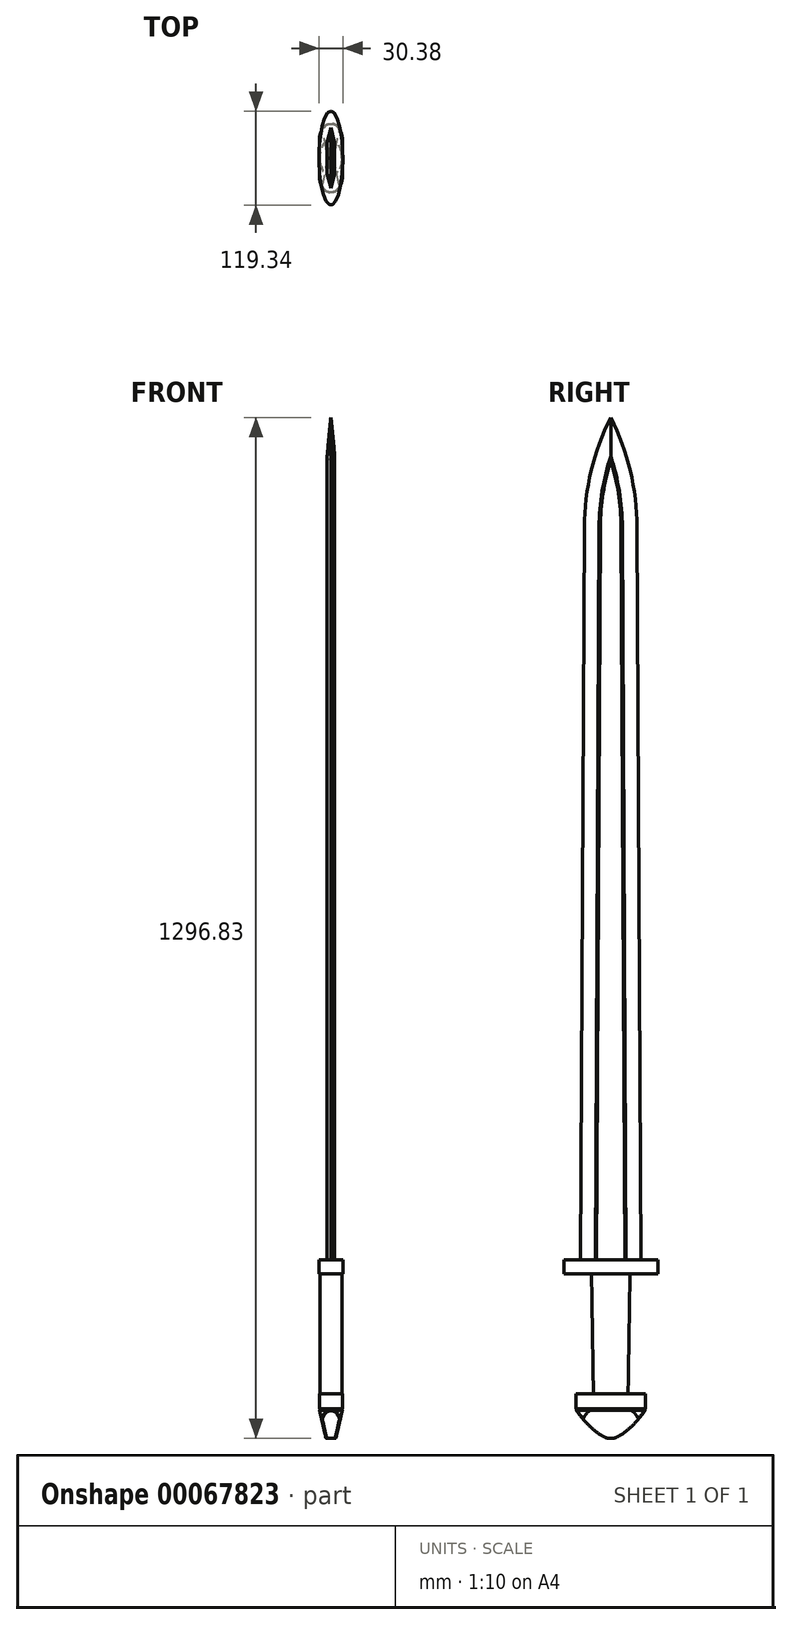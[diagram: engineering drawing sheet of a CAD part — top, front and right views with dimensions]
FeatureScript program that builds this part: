
annotation { "Feature Type Name" : "Feature", "Feature Type Description" : "" }
export const myFeature = defineFeature(function(context is Context, id is Id, definition is map)
    precondition{}
    {
        {
            var Q0;
            Q0=qCreatedBy(makeId("Top.planeOp"),FACE);
            var sketch = newSketch(context, id + "F0", { "sketchPlane" : qUnion([Q0])});
            skEllipse(sketch, "E0", {"center": v(0, 0) * mm, "majorRadius": 22.01 * mm, "minorRadius": 14.03 * mm, "majorAxis": v(0, 1)});
            skSolve(sketch);
        }
        {
            var Q0;
            Q0=makeQuery(id+"F0.imprint","IMPRINT",FACE,{"disambiguationData":[TD([[makeQuery(id+"F0.imprint","IMPRINT",EDGE,{"derivedFrom":sQuery(id+"F0.wireOp",EDGE,"E0")}),1.0]])]});
            cPlane(context, id + "F1", {"entities" : qUnion([Q0]), "cplaneType" : CPlaneType.OFFSET, "offset" : 152.4 * mm, "width" : 152.4 * mm, "height" : 152.4 * mm});
        }
        {
            var Q0;
            Q0=qCreatedBy(id+"F1.planeOp",FACE);
            var sketch = newSketch(context, id + "F2", { "sketchPlane" : qUnion([Q0])});
            skEllipse(sketch, "E1", {"center": v(0, 0) * mm, "majorRadius": 24.49 * mm, "minorRadius": 14.02 * mm, "majorAxis": v(0, 1)});
            skSolve(sketch);
        }
        {
            var Q0;
            Q0=makeQuery(id+"F0.imprint","IMPRINT",FACE,{"disambiguationData":[TD([[makeQuery(id+"F0.imprint","IMPRINT",EDGE,{"derivedFrom":sQuery(id+"F0.wireOp",EDGE,"E0")}),1.0]])]});
            var Q1;
            Q1=makeQuery(id+"F2.imprint","IMPRINT",FACE,{"disambiguationData":[TD([[makeQuery(id+"F2.imprint","IMPRINT",EDGE,{"derivedFrom":sQuery(id+"F2.wireOp",EDGE,"E1")}),1.0]])]});
            loft(context, id + "F3", {"sheetProfilesArray" : [{ "sheetProfileEntities" : qUnion([Q0]) }, { "sheetProfileEntities" : qUnion([Q1]) }]});
        }
        {
            var Q0;
            Q0=makeQuery(id+"F3.opLoft","CAP_FACE",FACE,{"disambiguationData":[OSD([makeQuery(id+"F2.imprint","IMPRINT",FACE,{"disambiguationData":[TD([[makeQuery(id+"F2.imprint","IMPRINT",EDGE,{"derivedFrom":sQuery(id+"F2.wireOp",EDGE,"E1")}),1.0]])]})])],"isStart":true});
            var sketch = newSketch(context, id + "F4", { "sketchPlane" : qUnion([Q0])});
            skEllipse(sketch, "E2", {"center": v(0, 0) * mm, "majorRadius": 50.25 * mm, "minorRadius": 14.05 * mm, "majorAxis": v(0, 1)});
            skEllipse(sketch, "E3", {"center": v(0, 0) * mm, "majorRadius": 59.67 * mm, "minorRadius": 15.2 * mm, "majorAxis": v(0, 1)});
            skSolve(sketch);
        }
        {
            var Q0;
            Q0 = qSketchRegion(id + "F4", true);
            var Q1;
            Q1=makeQuery(id+"F4.imprint","IMPRINT",FACE,{"disambiguationData":[TD([[makeQuery(id+"F4.imprint","IMPRINT",EDGE,{"derivedFrom":sQuery(id+"F4.wireOp",EDGE,"E2")}),1.0]])]});
            var Q2;
            Q2=makeQuery(id+"F4.imprint","IMPRINT",FACE,{"disambiguationData":[TD([[makeQuery(id+"F4.imprint","IMPRINT",EDGE,{"derivedFrom":makeQuery(id+"F3.opLoft","MID_CAP_EDGE",EDGE,{"disambiguationData":[OSD([sQuery(id+"F0.wireOp",EDGE,"E0"),sQuery(id+"F2.wireOp",EDGE,"E1")])],"capPos":1.0})}),1.0]])]});
            extrude(context, id + "F5", {"entities" : qUnion([Q0, Q1, Q2]), "depth" : 17.78 * mm});
        }
        {
            var Q0;
            Q0=makeQuery(id+"F3.opLoft","CAP_FACE",FACE,{"disambiguationData":[OSD([makeQuery(id+"F0.imprint","IMPRINT",FACE,{"disambiguationData":[TD([[makeQuery(id+"F0.imprint","IMPRINT",EDGE,{"derivedFrom":sQuery(id+"F0.wireOp",EDGE,"E0")}),1.0]])]})])],"isStart":true});
            var sketch = newSketch(context, id + "F6", { "sketchPlane" : qUnion([Q0])});
            skLineSegment(sketch, "E4.rect.left", {"start": v(-14.65, 22.86) * mm, "end": v(-14.65, -22.86) * mm});
            skLineSegment(sketch, "E4.rect.right", {"start": v(14.65, 22.86) * mm, "end": v(14.65, -22.86) * mm});
            skPoint(sketch, "E4.rect.middle", {"position": v(0, 0) * mm});
            skPoint(sketch, "E5.rect.middle", {"position": v(-14.65, 22.86) * mm});
            skEllipticalArc(sketch, "E6", {});
            skLineSegment(sketch, "E7", {"start": v(0, 0) * mm, "end": v(-5.94, 0) * mm});
            skEllipticalArc(sketch, "E8.MirrorCS", {});
            skPoint(sketch, "E5.rect.right.end.orphan", {"position": v(-43.96, 22.86) * mm});
            skPoint(sketch, "E5.rect.right.start.orphan", {"position": v(-47.78, 25.4) * mm});
            skPoint(sketch, "E5.rect.left.end.orphan", {"position": v(18.47, 20.32) * mm});
            const initialGuessF6  = {"E6": [0, 0.02286, -1, 0, 0.014653067193173231, 0.021324570960949005, 3.141592653589793, 6.283185307179586], "E8.MirrorCS": [0, -0.02286, -1, 0, 0.014653067193173231, 0.021324570960949005, 6.283185307179586, 3.141592653589793]};
            skSetInitialGuess(sketch, initialGuessF6);
            skSolve(sketch);
        }
        {
            var Q0;
            Q0 = qSketchRegion(id + "F6", true);
            extrude(context, id + "F7", {"entities" : qUnion([Q0]), "depth" : 20.32 * mm});
        }
        {
            var Q0;
            Q0=qCreatedBy(makeId("Right.planeOp"),FACE);
            var sketch = newSketch(context, id + "F8", { "sketchPlane" : qUnion([Q0])});
            skLineSegment(sketch, "E9.0", {"start": v(-44.18, -20.32) * mm, "end": v(-22.86, -20.32) * mm});
            skLineSegment(sketch, "E10.0", {"start": v(22.86, -20.32) * mm, "end": v(44.18, -20.32) * mm});
            skLineSegment(sketch, "E11", {"start": v(0, 0) * mm, "end": v(0, -64.5) * mm});
            skLineSegment(sketch, "E12", {"start": v(-10.54, -53.96) * mm, "end": v(-44.18, -20.32) * mm});
            skLineSegment(sketch, "E13", {"start": v(10.54, -53.96) * mm, "end": v(44.18, -20.32) * mm});
            skArc(sketch, "E14", {"start": v(-44.18, -20.32) * mm, "mid": v(-29.18, -38.96) * mm, "end": v(-10.54, -53.96) * mm});
            skArc(sketch, "E15.MirrorCS", {"start": v(44.18, -20.32) * mm, "mid": v(29.18, -38.96) * mm, "end": v(10.54, -53.96) * mm});
            skArc(sketch, "E16", {"start": v(-10.54, -53.96) * mm, "mid": v(0, -56.86) * mm, "end": v(10.54, -53.96) * mm});
            skLineSegment(sketch, "E17", {"start": v(-22.86, -20.32) * mm, "end": v(22.86, -20.32) * mm});
            skSolve(sketch);
        }
        {
            var Q0;
            Q0 = qSketchRegion(id + "F8", true);
            extrude(context, id + "F9", {"entities" : qUnion([Q0]), "operationType" : NewBodyOperationType.ADD, "endBound" : BoundingType.SYMMETRIC, "depth" : 29.46 * mm});
        }
        {
            var Q0;
            Q0=qCreatedBy(makeId("Front.planeOp"),FACE);
            cPlane(context, id + "F10", {"entities" : qUnion([Q0]), "cplaneType" : CPlaneType.OFFSET, "offset" : 152.4 * mm, "width" : 152.4 * mm, "height" : 152.4 * mm});
        }
        {
            var Q0;
            Q0=qCreatedBy(id+"F10.planeOp",FACE);
            var sketch = newSketch(context, id + "F11", { "sketchPlane" : qUnion([Q0])});
            skLineSegment(sketch, "E18.0", {"start": v(14.73, -20.32) * mm, "end": v(0, -20.32) * mm});
            skLineSegment(sketch, "E19", {"start": v(17.78, -56.86) * mm, "end": v(-17.78, -56.86) * mm});
            skLineSegment(sketch, "E20.0", {"start": v(0, -20.32) * mm, "end": v(-14.73, -20.32) * mm});
            skLineSegment(sketch, "E21", {"start": v(-17.78, -56.86) * mm, "end": v(-10.55, -20.32) * mm});
            skLineSegment(sketch, "E22", {"start": v(0, -20.32) * mm, "end": v(0, -24.34) * mm});
            skLineSegment(sketch, "E23.MirrorCS", {"start": v(17.78, -56.86) * mm, "end": v(10.55, -20.32) * mm});
            skPoint(sketch, "E24", {"position": v(-7.37, -20.32) * mm});
            skLineSegment(sketch, "E25.0", {"start": v(-14.73, -20.32) * mm, "end": v(-14.73, -53.96) * mm});
            skLineSegment(sketch, "E26.0", {"start": v(-14.73, -53.96) * mm, "end": v(-14.73, -56.86) * mm});
            skLineSegment(sketch, "E27.0", {"start": v(14.73, -53.96) * mm, "end": v(14.73, -56.86) * mm});
            skLineSegment(sketch, "E28.0", {"start": v(14.73, -20.32) * mm, "end": v(14.73, -53.96) * mm});
            skLineSegment(sketch, "E29", {"start": v(-14.73, -20.32) * mm, "end": v(-6.3, -56.86) * mm});
            skLineSegment(sketch, "E30.MirrorCS", {"start": v(14.73, -20.32) * mm, "end": v(6.3, -56.86) * mm});
            skSolve(sketch);
        }
        {
            var Q0;
            {var subQ0=sQuery(id+"F11.wireOp",EDGE,"E28.0");var subQ1=sQuery(id+"F11.wireOp",EDGE,"E23.MirrorCS");var subQ2=makeQuery(id+"F11.imprint","INTERSECT",VERTEX,{"derivedFrom":[subQ1,subQ0]});Q0=makeQuery(id+"F11.imprint","IMPRINT",FACE,{"disambiguationData":[TD([[makeQuery(id+"F11.imprint","IMPRINT",EDGE,{"disambiguationData":[TD([[subQ2,-1.0]])],"derivedFrom":subQ1}),-1.0]])]});}
            var Q1;
            {var subQ1=sQuery(id+"F11.wireOp",EDGE,"E27.0");Q1=makeQuery(id+"F11.imprint","IMPRINT",FACE,{"disambiguationData":[TD([[makeQuery(id+"F11.imprint","IMPRINT",EDGE,{"derivedFrom":subQ1}),-1.0]])]});}
            var Q2;
            {var subQ0=sQuery(id+"F11.wireOp",EDGE,"E26.0");Q2=makeQuery(id+"F11.imprint","IMPRINT",FACE,{"disambiguationData":[TD([[makeQuery(id+"F11.imprint","IMPRINT",EDGE,{"derivedFrom":subQ0}),1.0]])]});}
            var Q3;
            {var subQ0=sQuery(id+"F11.wireOp",EDGE,"E25.0");var subQ1=sQuery(id+"F11.wireOp",EDGE,"E21");var subQ2=makeQuery(id+"F11.imprint","INTERSECT",VERTEX,{"derivedFrom":[subQ1,subQ0]});Q3=makeQuery(id+"F11.imprint","IMPRINT",FACE,{"disambiguationData":[TD([[makeQuery(id+"F11.imprint","IMPRINT",EDGE,{"disambiguationData":[TD([[subQ2,-1.0]])],"derivedFrom":subQ1}),1.0]])]});}
            extrude(context, id + "F12", {"entities" : qUnion([Q0, Q1, Q2, Q3]), "operationType" : NewBodyOperationType.REMOVE, "endBound" : BoundingType.THROUGH_ALL, "oppositeDirection" : true, "depth" : 25.4 * mm});
        }
        {
            var Q0;
            Q0=makeQuery(id+"F7.opExtrude","CAP_FACE",FACE,{"disambiguationData":[OSD([sQuery(id+"F6.wireOp",EDGE,"E4.rect.left"),sQuery(id+"F6.wireOp",EDGE,"E4.rect.right"),sQuery(id+"F6.wireOp",EDGE,"E6"),sQuery(id+"F6.wireOp",EDGE,"E8.MirrorCS")])],"isStart":true});
            var sketch = newSketch(context, id + "F13", { "sketchPlane" : qUnion([Q0])});
            skLineSegment(sketch, "E31.0.0", {"start": v(-14.73, -44.18) * mm, "end": v(0, -44.18) * mm});
            skEllipticalArc(sketch, "E31.0.1", {});
            skLineSegment(sketch, "E31.0.2", {"start": v(-14.65, -22.86) * mm, "end": v(-14.65, 22.86) * mm});
            skEllipticalArc(sketch, "E31.0.3", {});
            skLineSegment(sketch, "E31.0.4", {"start": v(0, 44.18) * mm, "end": v(-14.73, 44.18) * mm});
            skLineSegment(sketch, "E31.0.5", {"start": v(-14.73, 44.18) * mm, "end": v(-14.73, -44.18) * mm});
            skLineSegment(sketch, "E32.0.0", {"start": v(14.65, 22.86) * mm, "end": v(14.65, -22.86) * mm});
            skEllipticalArc(sketch, "E32.0.1", {});
            skLineSegment(sketch, "E32.0.2", {"start": v(0, -44.18) * mm, "end": v(14.73, -44.18) * mm});
            skLineSegment(sketch, "E32.0.3", {"start": v(14.73, -44.18) * mm, "end": v(14.73, 44.18) * mm});
            skLineSegment(sketch, "E32.0.4", {"start": v(14.73, 44.18) * mm, "end": v(0, 44.18) * mm});
            skEllipticalArc(sketch, "E32.0.5", {});
            skEllipticalArc(sketch, "E33.0.0", {});
            skLineSegment(sketch, "E33.0.1", {"start": v(14.65, -22.86) * mm, "end": v(14.65, 22.86) * mm});
            skEllipticalArc(sketch, "E33.0.2", {});
            skLineSegment(sketch, "E33.0.3", {"start": v(-14.65, 22.86) * mm, "end": v(-14.65, -22.86) * mm});
            const initialGuessF13  = {"E31.0.1": [0, -0.02286, 0, 1, 0.021324570960949005, 0.014653067193173231, 1.5707963267948966, 3.141592653589793], "E31.0.3": [0, 0.02286, 0, 1, 0.021324570960949005, 0.014653067193173231, 0, 1.5707963267948966], "E32.0.1": [0, -0.02286, 0, 1, 0.021324570960949005, 0.014653067193173231, 3.141592653589793, 4.71238898038469], "E32.0.5": [0, 0.02286, 0, 1, 0.021324570960949005, 0.014653067193173231, 4.71238898038469, 0], "E33.0.0": [0, -0.02286, 0, 1, 0.021324570960949005, 0.014653067193173231, 1.5707963267948966, 4.71238898038469], "E33.0.2": [0, 0.02286, 0, 1, 0.021324570960949005, 0.014653067193173231, 4.71238898038469, 1.5707963267948966]};
            skSetInitialGuess(sketch, initialGuessF13);
            skSolve(sketch);
        }
        {
            var Q0;
            {var subQ3=sQuery(id+"F13.wireOp",EDGE,"E31.0.0");Q0=makeQuery(id+"F13.imprint","IMPRINT",FACE,{"disambiguationData":[TD([[makeQuery(id+"F13.imprint","IMPRINT",EDGE,{"derivedFrom":subQ3}),1.0]])]});}
            var Q1;
            {var subQ3=sQuery(id+"F13.wireOp",EDGE,"E32.0.2");Q1=makeQuery(id+"F13.imprint","IMPRINT",FACE,{"disambiguationData":[TD([[makeQuery(id+"F13.imprint","IMPRINT",EDGE,{"derivedFrom":subQ3}),1.0]])]});}
            extrude(context, id + "F14", {"entities" : qUnion([Q0, Q1]), "operationType" : NewBodyOperationType.REMOVE, "endBound" : BoundingType.THROUGH_ALL, "oppositeDirection" : true, "depth" : 25.4 * mm});
        }
        {
            var Q0;
            Q0=makeQuery(id+"F7.opExtrude","CAP_FACE",FACE,{"disambiguationData":[OSD([sQuery(id+"F6.wireOp",EDGE,"E4.rect.left"),sQuery(id+"F6.wireOp",EDGE,"E4.rect.right"),sQuery(id+"F6.wireOp",EDGE,"E6"),sQuery(id+"F6.wireOp",EDGE,"E8.MirrorCS")])],"isStart":true});
            cPlane(context, id + "F15", {"entities" : qUnion([Q0]), "cplaneType" : CPlaneType.OFFSET, "offset" : 20.32 * mm, "oppositeDirection" : true, "width" : 152.4 * mm, "height" : 152.4 * mm});
        }
        {
            var Q0;
            Q0=qCreatedBy(id+"F15.planeOp",FACE);
            var sketch = newSketch(context, id + "F16", { "sketchPlane" : qUnion([Q0])});
            skEllipticalArc(sketch, "E34.0.0", {});
            skLineSegment(sketch, "E34.0.1", {"start": v(14.65, -22.86) * mm, "end": v(14.65, 22.86) * mm});
            skEllipticalArc(sketch, "E34.0.2", {});
            skLineSegment(sketch, "E34.0.3", {"start": v(-14.65, 22.86) * mm, "end": v(-14.65, -22.86) * mm});
            skLineSegment(sketch, "E35", {"start": v(-14.65, 22.86) * mm, "end": v(14.65, 22.86) * mm});
            skLineSegment(sketch, "E36", {"start": v(14.65, -22.86) * mm, "end": v(-14.65, -22.86) * mm});
            skPoint(sketch, "E37", {"position": v(0, 44.18) * mm});
            skPoint(sketch, "E38", {"position": v(0, -44.18) * mm});
            skEllipse(sketch, "E39", {"center": v(0, 22.86) * mm, "majorRadius": 21.32 * mm, "minorRadius": 14.65 * mm, "majorAxis": v(0, 1)});
            skEllipse(sketch, "E40", {"center": v(0, -22.86) * mm, "majorRadius": 21.32 * mm, "minorRadius": 14.65 * mm, "majorAxis": v(0, -1)});
            skPoint(sketch, "E41", {"position": v(-14.65, 0) * mm});
            const initialGuessF16  = {"E34.0.0": [0, -0.02286, 0, 1, 0.021324570960949005, 0.014653067193173231, 1.5707963267948966, 4.71238898038469], "E34.0.2": [0, 0.02286, 0, 1, 0.021324570960949005, 0.014653067193173231, 4.71238898038469, 1.5707963267948966], "E34.0.0": [0, -0.02286, 0, 1, 0.021324570960949005, 0.014653067193173231, 1.5707963267948966, 4.71238898038469], "E34.0.2": [0, 0.02286, 0, 1, 0.021324570960949005, 0.014653067193173231, 4.71238898038469, 1.5707963267948966]};
            skSetInitialGuess(sketch, initialGuessF16);
            skSolve(sketch);
        }
        {
            var Q0;
            Q0=qCreatedBy(makeId("Front.planeOp"),FACE);
            var sketch = newSketch(context, id + "F17", { "sketchPlane" : qUnion([Q0])});
            skPoint(sketch, "E42.0", {"position": v(-14.65, -20.32) * mm});
            skCircle(sketch, "E43", {"center": v(-14.65, -20.32) * mm, "radius": 0.94 * mm});
            skPoint(sketch, "E44.0", {"position": v(14.65, -20.32) * mm});
            skCircle(sketch, "E45", {"center": v(14.65, -20.32) * mm, "radius": 0.94 * mm});
            skPoint(sketch, "E46.0", {"position": v(7.02, -20.73) * mm});
            skPoint(sketch, "E47.0", {"position": v(36.33, -20.73) * mm});
            skSolve(sketch);
        }
        {
            var Q0;
            Q0=qCreatedBy(makeId("Front.planeOp"),FACE);
            cPlane(context, id + "F18", {"entities" : qUnion([Q0]), "cplaneType" : CPlaneType.OFFSET, "offset" : 22.86 * mm, "width" : 152.4 * mm, "height" : 152.4 * mm});
        }
        {
            var Q0;
            Q0=qCreatedBy(id+"F18.planeOp",FACE);
            var sketch = newSketch(context, id + "F19", { "sketchPlane" : qUnion([Q0])});
            skCircle(sketch, "E48.0", {"center": v(-14.65, -20.32) * mm, "radius": 0.94 * mm});
            skSolve(sketch);
        }
        {
            var Q0;
            Q0=qCreatedBy(id+"F18.planeOp",FACE);
            cPlane(context, id + "F20", {"entities" : qUnion([Q0]), "cplaneType" : CPlaneType.OFFSET, "offset" : 45.72 * mm, "oppositeDirection" : true, "width" : 152.4 * mm, "height" : 152.4 * mm});
        }
        {
            var Q0;
            Q0=qCreatedBy(id+"F20.planeOp",FACE);
            var sketch = newSketch(context, id + "F21", { "sketchPlane" : qUnion([Q0])});
            skCircle(sketch, "E49.0", {"center": v(-14.65, -20.32) * mm, "radius": 0.94 * mm});
            skSolve(sketch);
        }
        {
            var Q0;
            Q0=makeQuery(id+"F21.imprint","IMPRINT",FACE,{"disambiguationData":[TD([[makeQuery(id+"F21.imprint","IMPRINT",EDGE,{"derivedFrom":sQuery(id+"F21.wireOp",EDGE,"E49.0")}),1.0]])]});
            var Q1;
            Q1=sQuery(id+"F16.wireOp",EDGE,"E34.0.2");
            sweep(context, id + "F22", {"operationType" : NewBodyOperationType.REMOVE, "profiles" : qUnion([Q0]), "path" : qUnion([Q1])});
        }
        {
            var Q0;
            Q0=makeQuery(id+"F19.imprint","IMPRINT",FACE,{"disambiguationData":[TD([[makeQuery(id+"F19.imprint","IMPRINT",EDGE,{"derivedFrom":sQuery(id+"F19.wireOp",EDGE,"E48.0")}),1.0]])]});
            var Q1;
            Q1=sQuery(id+"F16.wireOp",EDGE,"E34.0.0");
            sweep(context, id + "F23", {"operationType" : NewBodyOperationType.REMOVE, "profiles" : qUnion([Q0]), "path" : qUnion([Q1])});
        }
        {
            var Q0;
            Q0=makeQuery(id+"F17.imprint","IMPRINT",FACE,{"disambiguationData":[TD([[makeQuery(id+"F17.imprint","IMPRINT",EDGE,{"derivedFrom":sQuery(id+"F17.wireOp",EDGE,"E43")}),1.0]])]});
            extrude(context, id + "F24", {"entities" : qUnion([Q0]), "operationType" : NewBodyOperationType.REMOVE, "endBound" : BoundingType.SYMMETRIC, "oppositeDirection" : true, "depth" : 254 * mm});
        }
        {
            var Q0;
            Q0=makeQuery(id+"F17.imprint","IMPRINT",FACE,{"disambiguationData":[TD([[makeQuery(id+"F17.imprint","IMPRINT",EDGE,{"derivedFrom":sQuery(id+"F17.wireOp",EDGE,"E45")}),1.0]])]});
            extrude(context, id + "F25", {"entities" : qUnion([Q0]), "operationType" : NewBodyOperationType.REMOVE, "endBound" : BoundingType.SYMMETRIC, "depth" : 254 * mm});
        }
        {
            var Q0;
            Q0=qCreatedBy(makeId("Right.planeOp"),FACE);
            var sketch = newSketch(context, id + "F26", { "sketchPlane" : qUnion([Q0])});
            skArc(sketch, "E50.0", {"start": v(10.54, -53.96) * mm, "mid": v(0, -56.86) * mm, "end": v(-10.54, -53.96) * mm});
            skLineSegment(sketch, "E51.0", {"start": v(-59.67, 170.18) * mm, "end": v(59.67, 170.18) * mm});
            skLineSegment(sketch, "E52", {"start": v(0, 170.18) * mm, "end": v(0, 1109.98) * mm});
            skLineSegment(sketch, "E53", {"start": v(38.35, 170.18) * mm, "end": v(33.47, 1100.69) * mm});
            skLineSegment(sketch, "E54.MirrorCS", {"start": v(-38.35, 170.18) * mm, "end": v(-33.47, 1100.69) * mm});
            skLineSegment(sketch, "E55", {"start": v(0, 1109.98) * mm, "end": v(0, 1239.97) * mm});
            skArc(sketch, "E56", {"start": v(33.47, 1100.69) * mm, "mid": v(24.8, 1172.27) * mm, "end": v(0, 1239.97) * mm});
            skArc(sketch, "E57.MirrorCS", {"start": v(-33.47, 1100.69) * mm, "mid": v(-24.8, 1172.27) * mm, "end": v(0, 1239.97) * mm});
            skSolve(sketch);
        }
        {
            var Q0;
            Q0 = qSketchRegion(id + "F26", true);
            extrude(context, id + "F27", {"entities" : qUnion([Q0]), "endBound" : BoundingType.SYMMETRIC, "depth" : 10.16 * mm});
        }
        {
            var Q0;
            Q0=makeQuery(id+"F27.opExtrude","CAP_EDGE",EDGE,{"disambiguationData":[OSD([sQuery(id+"F26.wireOp",EDGE,"E53")])],"isStart":true});
            var Q1;
            Q1=makeQuery(id+"F27.opExtrude","CAP_EDGE",EDGE,{"disambiguationData":[OSD([sQuery(id+"F26.wireOp",EDGE,"E54.MirrorCS")])],"isStart":true});
            chamfer(context, id + "F28", {"entities" : qUnion([Q0, Q1]), "chamferType" : ChamferType.TWO_OFFSETS, "width1" : 5.08 * mm, "oppositeDirection" : false, "width2" : 20.32 * mm, "tangentPropagation" : true});
        }
        {
            var Q0;
            Q0=makeQuery(id+"F27.opExtrude","CAP_EDGE",EDGE,{"disambiguationData":[OSD([sQuery(id+"F26.wireOp",EDGE,"E54.MirrorCS")])],"isStart":false});
            var Q1;
            Q1=makeQuery(id+"F27.opExtrude","CAP_EDGE",EDGE,{"disambiguationData":[OSD([sQuery(id+"F26.wireOp",EDGE,"E53")])],"isStart":false});
            chamfer(context, id + "F29", {"entities" : qUnion([Q0, Q1]), "chamferType" : ChamferType.TWO_OFFSETS, "width1" : 5.08 * mm, "oppositeDirection" : false, "width2" : 20.32 * mm, "tangentPropagation" : true});
        }
        {
            var Q0;
            Q0=makeQuery(id+"F27.opExtrude","CAP_FACE",FACE,{"disambiguationData":[OSD([sQuery(id+"F26.wireOp",EDGE,"E51.0"),sQuery(id+"F26.wireOp",EDGE,"E53"),sQuery(id+"F26.wireOp",EDGE,"E54.MirrorCS"),sQuery(id+"F26.wireOp",EDGE,"E56"),sQuery(id+"F26.wireOp",EDGE,"E57.MirrorCS")])],"isStart":false});
            var sketch = newSketch(context, id + "F30", { "sketchPlane" : qUnion([Q0])});
            skLineSegment(sketch, "E58.0.0", {"start": v(-18.03, 170.18) * mm, "end": v(18.03, 170.18) * mm});
            skLineSegment(sketch, "E58.0.1", {"start": v(18.03, 170.18) * mm, "end": v(13.15, 1100.58) * mm});
            skArc(sketch, "E58.0.2", {"start": v(13.15, 1100.58) * mm, "mid": v(9.73, 1143.71) * mm, "end": v(0, 1185.87) * mm});
            skArc(sketch, "E58.0.3", {"start": v(0, 1185.87) * mm, "mid": v(-9.73, 1143.71) * mm, "end": v(-13.15, 1100.58) * mm});
            skLineSegment(sketch, "E58.0.4", {"start": v(-13.15, 1100.58) * mm, "end": v(-18.03, 170.18) * mm});
            skSolve(sketch);
        }
        {
            var Q0;
            Q0 = qSketchRegion(id + "F30", true);
            extrude(context, id + "F31", {"entities" : qUnion([Q0]), "operationType" : NewBodyOperationType.REMOVE, "oppositeDirection" : true, "depth" : 2.54 * mm});
        }
        {
            var Q0;
            Q0=makeQuery(id+"F27.opExtrude","CAP_FACE",FACE,{"disambiguationData":[OSD([sQuery(id+"F26.wireOp",EDGE,"E51.0"),sQuery(id+"F26.wireOp",EDGE,"E53"),sQuery(id+"F26.wireOp",EDGE,"E54.MirrorCS"),sQuery(id+"F26.wireOp",EDGE,"E56"),sQuery(id+"F26.wireOp",EDGE,"E57.MirrorCS")])],"isStart":true});
            var sketch = newSketch(context, id + "F32", { "sketchPlane" : qUnion([Q0])});
            skLineSegment(sketch, "E59.0.0", {"start": v(-18.03, 170.18) * mm, "end": v(18.03, 170.18) * mm});
            skLineSegment(sketch, "E59.0.1", {"start": v(18.03, 170.18) * mm, "end": v(13.15, 1100.58) * mm});
            skArc(sketch, "E59.0.2", {"start": v(13.15, 1100.58) * mm, "mid": v(9.73, 1143.71) * mm, "end": v(0, 1185.87) * mm});
            skArc(sketch, "E59.0.3", {"start": v(0, 1185.87) * mm, "mid": v(-9.73, 1143.71) * mm, "end": v(-13.15, 1100.58) * mm});
            skLineSegment(sketch, "E59.0.4", {"start": v(-13.15, 1100.58) * mm, "end": v(-18.03, 170.18) * mm});
            skSolve(sketch);
        }
        {
            var Q0;
            Q0 = qSketchRegion(id + "F32", true);
            extrude(context, id + "F33", {"entities" : qUnion([Q0]), "operationType" : NewBodyOperationType.REMOVE, "oppositeDirection" : true, "depth" : 2.54 * mm});
        }
        {
            var Q0;
            Q0=makeQuery(id+"F31.boolean.opBoolean","COPY",FACE,{"derivedFrom":makeQuery(id+"F31.opExtrude","CAP_FACE",FACE,{"disambiguationData":[OSD([sQuery(id+"F30.wireOp",EDGE,"E58.0.0"),sQuery(id+"F30.wireOp",EDGE,"E58.0.1"),sQuery(id+"F30.wireOp",EDGE,"E58.0.2"),sQuery(id+"F30.wireOp",EDGE,"E58.0.3"),sQuery(id+"F30.wireOp",EDGE,"E58.0.4")])],"isStart":false})});
            var sketch = newSketch(context, id + "F34", { "sketchPlane" : qUnion([Q0])});
            skLineSegment(sketch, "E60.0.0", {"start": v(-13.15, 1100.58) * mm, "end": v(-18.03, 170.18) * mm});
            skLineSegment(sketch, "E60.0.1", {"start": v(-18.03, 170.18) * mm, "end": v(18.03, 170.18) * mm});
            skLineSegment(sketch, "E60.0.2", {"start": v(18.03, 170.18) * mm, "end": v(13.15, 1100.58) * mm});
            skArc(sketch, "E60.0.3", {"start": v(13.15, 1100.58) * mm, "mid": v(9.73, 1143.71) * mm, "end": v(0, 1185.87) * mm});
            skArc(sketch, "E60.0.4", {"start": v(0, 1185.87) * mm, "mid": v(-9.73, 1143.71) * mm, "end": v(-13.15, 1100.58) * mm});
            skSolve(sketch);
        }
        {
            var Q0;
            Q0 = qSketchRegion(id + "F34", true);
            extrude(context, id + "F35", {"entities" : qUnion([Q0]), "depth" : 1.27 * mm});
        }
        {
            var Q0;
            Q0=makeQuery(id+"F33.boolean.opBoolean","COPY",FACE,{"derivedFrom":makeQuery(id+"F33.opExtrude","CAP_FACE",FACE,{"disambiguationData":[OSD([sQuery(id+"F32.wireOp",EDGE,"E59.0.0"),sQuery(id+"F32.wireOp",EDGE,"E59.0.1"),sQuery(id+"F32.wireOp",EDGE,"E59.0.2"),sQuery(id+"F32.wireOp",EDGE,"E59.0.3"),sQuery(id+"F32.wireOp",EDGE,"E59.0.4")])],"isStart":false})});
            var sketch = newSketch(context, id + "F36", { "sketchPlane" : qUnion([Q0])});
            skLineSegment(sketch, "E61.0.0", {"start": v(-18.03, 170.18) * mm, "end": v(18.03, 170.18) * mm});
            skLineSegment(sketch, "E61.0.1", {"start": v(18.03, 170.18) * mm, "end": v(13.15, 1100.58) * mm});
            skArc(sketch, "E61.0.2", {"start": v(13.15, 1100.58) * mm, "mid": v(9.73, 1143.71) * mm, "end": v(0, 1185.87) * mm});
            skArc(sketch, "E61.0.3", {"start": v(0, 1185.87) * mm, "mid": v(-9.73, 1143.71) * mm, "end": v(-13.15, 1100.58) * mm});
            skLineSegment(sketch, "E61.0.4", {"start": v(-13.15, 1100.58) * mm, "end": v(-18.03, 170.18) * mm});
            skSolve(sketch);
        }
        {
            var Q0;
            Q0 = qSketchRegion(id + "F36", true);
            extrude(context, id + "F37", {"entities" : qUnion([Q0]), "depth" : 1.27 * mm});
        }
        {
            var Q0;
            {var subQ0=sQuery(id+"F26.wireOp",EDGE,"E54.MirrorCS");Q0=makeQuery(id+"F31.boolean.opBoolean","MERGE",EDGE,{"derivedFrom":[makeQuery(id+"F29.opChamfer","BLEND_EDGE",EDGE,{"blendedFrom":[makeQuery(id+"F27.opExtrude","CAP_EDGE",EDGE,{"disambiguationData":[OSD([subQ0])],"isStart":false}),makeQuery(id+"F27.opExtrude","CAP_FACE",FACE,{"disambiguationData":[OSD([sQuery(id+"F26.wireOp",EDGE,"E51.0"),sQuery(id+"F26.wireOp",EDGE,"E53"),subQ0,sQuery(id+"F26.wireOp",EDGE,"E56"),sQuery(id+"F26.wireOp",EDGE,"E57.MirrorCS")])],"isStart":false})],"blendedInto":[makeQuery(id+"F27.opExtrude","CAP_FACE",FACE,{"disambiguationData":[OSD([sQuery(id+"F26.wireOp",EDGE,"E51.0"),sQuery(id+"F26.wireOp",EDGE,"E53"),subQ0,sQuery(id+"F26.wireOp",EDGE,"E56"),sQuery(id+"F26.wireOp",EDGE,"E57.MirrorCS")])],"isStart":false})]}),makeQuery(id+"F31.opExtrude","CAP_EDGE",EDGE,{"disambiguationData":[OSD([sQuery(id+"F30.wireOp",EDGE,"E58.0.4")])],"isStart":true})]});}
            var Q1;
            {var subQ0=sQuery(id+"F26.wireOp",EDGE,"E57.MirrorCS");Q1=makeQuery(id+"F31.boolean.opBoolean","MERGE",EDGE,{"derivedFrom":[makeQuery(id+"F29.opChamfer","BLEND_EDGE",EDGE,{"blendedFrom":[makeQuery(id+"F27.opExtrude","CAP_EDGE",EDGE,{"disambiguationData":[OSD([subQ0])],"isStart":false}),makeQuery(id+"F27.opExtrude","CAP_FACE",FACE,{"disambiguationData":[OSD([sQuery(id+"F26.wireOp",EDGE,"E51.0"),sQuery(id+"F26.wireOp",EDGE,"E53"),sQuery(id+"F26.wireOp",EDGE,"E54.MirrorCS"),sQuery(id+"F26.wireOp",EDGE,"E56"),subQ0])],"isStart":false})],"blendedInto":[makeQuery(id+"F27.opExtrude","CAP_FACE",FACE,{"disambiguationData":[OSD([sQuery(id+"F26.wireOp",EDGE,"E51.0"),sQuery(id+"F26.wireOp",EDGE,"E53"),sQuery(id+"F26.wireOp",EDGE,"E54.MirrorCS"),sQuery(id+"F26.wireOp",EDGE,"E56"),subQ0])],"isStart":false})]}),makeQuery(id+"F31.opExtrude","CAP_EDGE",EDGE,{"disambiguationData":[OSD([sQuery(id+"F30.wireOp",EDGE,"E58.0.3")])],"isStart":true})]});}
            var Q2;
            {var subQ0=sQuery(id+"F26.wireOp",EDGE,"E54.MirrorCS");Q2=makeQuery(id+"F33.boolean.opBoolean","MERGE",EDGE,{"derivedFrom":[makeQuery(id+"F28.opChamfer","BLEND_EDGE",EDGE,{"blendedFrom":[makeQuery(id+"F27.opExtrude","CAP_EDGE",EDGE,{"disambiguationData":[OSD([subQ0])],"isStart":true}),makeQuery(id+"F27.opExtrude","CAP_FACE",FACE,{"disambiguationData":[OSD([sQuery(id+"F26.wireOp",EDGE,"E51.0"),sQuery(id+"F26.wireOp",EDGE,"E53"),subQ0,sQuery(id+"F26.wireOp",EDGE,"E56"),sQuery(id+"F26.wireOp",EDGE,"E57.MirrorCS")])],"isStart":true})],"blendedInto":[makeQuery(id+"F27.opExtrude","CAP_FACE",FACE,{"disambiguationData":[OSD([sQuery(id+"F26.wireOp",EDGE,"E51.0"),sQuery(id+"F26.wireOp",EDGE,"E53"),subQ0,sQuery(id+"F26.wireOp",EDGE,"E56"),sQuery(id+"F26.wireOp",EDGE,"E57.MirrorCS")])],"isStart":true})]}),makeQuery(id+"F33.opExtrude","CAP_EDGE",EDGE,{"disambiguationData":[OSD([sQuery(id+"F32.wireOp",EDGE,"E59.0.1")])],"isStart":true})]});}
            var Q3;
            {var subQ0=sQuery(id+"F26.wireOp",EDGE,"E57.MirrorCS");Q3=makeQuery(id+"F33.boolean.opBoolean","MERGE",EDGE,{"derivedFrom":[makeQuery(id+"F28.opChamfer","BLEND_EDGE",EDGE,{"blendedFrom":[makeQuery(id+"F27.opExtrude","CAP_EDGE",EDGE,{"disambiguationData":[OSD([subQ0])],"isStart":true}),makeQuery(id+"F27.opExtrude","CAP_FACE",FACE,{"disambiguationData":[OSD([sQuery(id+"F26.wireOp",EDGE,"E51.0"),sQuery(id+"F26.wireOp",EDGE,"E53"),sQuery(id+"F26.wireOp",EDGE,"E54.MirrorCS"),sQuery(id+"F26.wireOp",EDGE,"E56"),subQ0])],"isStart":true})],"blendedInto":[makeQuery(id+"F27.opExtrude","CAP_FACE",FACE,{"disambiguationData":[OSD([sQuery(id+"F26.wireOp",EDGE,"E51.0"),sQuery(id+"F26.wireOp",EDGE,"E53"),sQuery(id+"F26.wireOp",EDGE,"E54.MirrorCS"),sQuery(id+"F26.wireOp",EDGE,"E56"),subQ0])],"isStart":true})]}),makeQuery(id+"F33.opExtrude","CAP_EDGE",EDGE,{"disambiguationData":[OSD([sQuery(id+"F32.wireOp",EDGE,"E59.0.2")])],"isStart":true})]});}
            chamfer(context, id + "F38", {"entities" : qUnion([Q0, Q1, Q2, Q3]), "width" : 1.27 * mm, "tangentPropagation" : true});
        }
        {
            var Q0;
            {var subQ0=sQuery(id+"F26.wireOp",EDGE,"E56");Q0=makeQuery(id+"F33.boolean.opBoolean","MERGE",EDGE,{"derivedFrom":[makeQuery(id+"F28.opChamfer","BLEND_EDGE",EDGE,{"blendedFrom":[makeQuery(id+"F27.opExtrude","CAP_EDGE",EDGE,{"disambiguationData":[OSD([subQ0])],"isStart":true}),makeQuery(id+"F27.opExtrude","CAP_FACE",FACE,{"disambiguationData":[OSD([sQuery(id+"F26.wireOp",EDGE,"E51.0"),sQuery(id+"F26.wireOp",EDGE,"E53"),sQuery(id+"F26.wireOp",EDGE,"E54.MirrorCS"),subQ0,sQuery(id+"F26.wireOp",EDGE,"E57.MirrorCS")])],"isStart":true})],"blendedInto":[makeQuery(id+"F27.opExtrude","CAP_FACE",FACE,{"disambiguationData":[OSD([sQuery(id+"F26.wireOp",EDGE,"E51.0"),sQuery(id+"F26.wireOp",EDGE,"E53"),sQuery(id+"F26.wireOp",EDGE,"E54.MirrorCS"),subQ0,sQuery(id+"F26.wireOp",EDGE,"E57.MirrorCS")])],"isStart":true})]}),makeQuery(id+"F33.opExtrude","CAP_EDGE",EDGE,{"disambiguationData":[OSD([sQuery(id+"F32.wireOp",EDGE,"E59.0.3")])],"isStart":true})]});}
            var Q1;
            {var subQ0=sQuery(id+"F26.wireOp",EDGE,"E53");Q1=makeQuery(id+"F33.boolean.opBoolean","MERGE",EDGE,{"derivedFrom":[makeQuery(id+"F28.opChamfer","BLEND_EDGE",EDGE,{"blendedFrom":[makeQuery(id+"F27.opExtrude","CAP_EDGE",EDGE,{"disambiguationData":[OSD([subQ0])],"isStart":true}),makeQuery(id+"F27.opExtrude","CAP_FACE",FACE,{"disambiguationData":[OSD([sQuery(id+"F26.wireOp",EDGE,"E51.0"),subQ0,sQuery(id+"F26.wireOp",EDGE,"E54.MirrorCS"),sQuery(id+"F26.wireOp",EDGE,"E56"),sQuery(id+"F26.wireOp",EDGE,"E57.MirrorCS")])],"isStart":true})],"blendedInto":[makeQuery(id+"F27.opExtrude","CAP_FACE",FACE,{"disambiguationData":[OSD([sQuery(id+"F26.wireOp",EDGE,"E51.0"),subQ0,sQuery(id+"F26.wireOp",EDGE,"E54.MirrorCS"),sQuery(id+"F26.wireOp",EDGE,"E56"),sQuery(id+"F26.wireOp",EDGE,"E57.MirrorCS")])],"isStart":true})]}),makeQuery(id+"F33.opExtrude","CAP_EDGE",EDGE,{"disambiguationData":[OSD([sQuery(id+"F32.wireOp",EDGE,"E59.0.4")])],"isStart":true})]});}
            var Q2;
            {var subQ0=sQuery(id+"F26.wireOp",EDGE,"E56");Q2=makeQuery(id+"F31.boolean.opBoolean","MERGE",EDGE,{"derivedFrom":[makeQuery(id+"F29.opChamfer","BLEND_EDGE",EDGE,{"blendedFrom":[makeQuery(id+"F27.opExtrude","CAP_EDGE",EDGE,{"disambiguationData":[OSD([subQ0])],"isStart":false}),makeQuery(id+"F27.opExtrude","CAP_FACE",FACE,{"disambiguationData":[OSD([sQuery(id+"F26.wireOp",EDGE,"E51.0"),sQuery(id+"F26.wireOp",EDGE,"E53"),sQuery(id+"F26.wireOp",EDGE,"E54.MirrorCS"),subQ0,sQuery(id+"F26.wireOp",EDGE,"E57.MirrorCS")])],"isStart":false})],"blendedInto":[makeQuery(id+"F27.opExtrude","CAP_FACE",FACE,{"disambiguationData":[OSD([sQuery(id+"F26.wireOp",EDGE,"E51.0"),sQuery(id+"F26.wireOp",EDGE,"E53"),sQuery(id+"F26.wireOp",EDGE,"E54.MirrorCS"),subQ0,sQuery(id+"F26.wireOp",EDGE,"E57.MirrorCS")])],"isStart":false})]}),makeQuery(id+"F31.opExtrude","CAP_EDGE",EDGE,{"disambiguationData":[OSD([sQuery(id+"F30.wireOp",EDGE,"E58.0.2")])],"isStart":true})]});}
            var Q3;
            {var subQ0=sQuery(id+"F26.wireOp",EDGE,"E53");Q3=makeQuery(id+"F31.boolean.opBoolean","MERGE",EDGE,{"derivedFrom":[makeQuery(id+"F29.opChamfer","BLEND_EDGE",EDGE,{"blendedFrom":[makeQuery(id+"F27.opExtrude","CAP_EDGE",EDGE,{"disambiguationData":[OSD([subQ0])],"isStart":false}),makeQuery(id+"F27.opExtrude","CAP_FACE",FACE,{"disambiguationData":[OSD([sQuery(id+"F26.wireOp",EDGE,"E51.0"),subQ0,sQuery(id+"F26.wireOp",EDGE,"E54.MirrorCS"),sQuery(id+"F26.wireOp",EDGE,"E56"),sQuery(id+"F26.wireOp",EDGE,"E57.MirrorCS")])],"isStart":false})],"blendedInto":[makeQuery(id+"F27.opExtrude","CAP_FACE",FACE,{"disambiguationData":[OSD([sQuery(id+"F26.wireOp",EDGE,"E51.0"),subQ0,sQuery(id+"F26.wireOp",EDGE,"E54.MirrorCS"),sQuery(id+"F26.wireOp",EDGE,"E56"),sQuery(id+"F26.wireOp",EDGE,"E57.MirrorCS")])],"isStart":false})]}),makeQuery(id+"F31.opExtrude","CAP_EDGE",EDGE,{"disambiguationData":[OSD([sQuery(id+"F30.wireOp",EDGE,"E58.0.1")])],"isStart":true})]});}
            chamfer(context, id + "F39", {"entities" : qUnion([Q0, Q1, Q2, Q3]), "width" : 1.27 * mm, "tangentPropagation" : true});
        }
        {
            var Q0;
            Q0=qCreatedBy(makeId("Right.planeOp"),FACE);
            var sketch = newSketch(context, id + "F40", { "sketchPlane" : qUnion([Q0])});
            skLineSegment(sketch, "E62.0", {"start": v(-18.03, 170.18) * mm, "end": v(18.03, 170.18) * mm});
            skLineSegment(sketch, "E63.0", {"start": v(-19.26, 170.18) * mm, "end": v(-38.35, 170.18) * mm});
            skLineSegment(sketch, "E64.0", {"start": v(-18.03, 170.18) * mm, "end": v(-19.26, 170.18) * mm});
            skLineSegment(sketch, "E65.0", {"start": v(19.26, 170.18) * mm, "end": v(18.03, 170.18) * mm});
            skLineSegment(sketch, "E66.0", {"start": v(38.35, 170.18) * mm, "end": v(19.26, 170.18) * mm});
            skLineSegment(sketch, "E67", {"start": v(-20.88, 170.18) * mm, "end": v(-10.86, -33.64) * mm});
            skLineSegment(sketch, "E68", {"start": v(0, 0) * mm, "end": v(0, 12.98) * mm});
            skLineSegment(sketch, "E69.MirrorCS", {"start": v(20.88, 170.18) * mm, "end": v(10.86, -33.64) * mm});
            skLineSegment(sketch, "E70", {"start": v(-10.86, -33.64) * mm, "end": v(10.86, -33.64) * mm});
            skSolve(sketch);
        }
        {
            var Q0;
            Q0 = qSketchRegion(id + "F40", true);
            extrude(context, id + "F41", {"entities" : qUnion([Q0]), "operationType" : NewBodyOperationType.REMOVE, "endBound" : BoundingType.SYMMETRIC, "oppositeDirection" : true, "depth" : 7.11 * mm});
        }
        {
            var Q0;
            Q0=makeQuery(id+"F40.imprint","IMPRINT",FACE,{"disambiguationData":[TD([[makeQuery(id+"F40.imprint","IMPRINT",EDGE,{"derivedFrom":sQuery(id+"F40.wireOp",EDGE,"E62.0")}),-1.0]])]});
            extrude(context, id + "F42", {"entities" : qUnion([Q0]), "operationType" : NewBodyOperationType.ADD, "endBound" : BoundingType.SYMMETRIC, "depth" : 7.11 * mm});
        }
        {
            var Q0;
            Q0=makeQuery(id+"F9.opExtrude","SWEPT_FACE",FACE,{"disambiguationData":[OSD([sQuery(id+"F8.wireOp",EDGE,"E15.MirrorCS")])]});
            var Q1;
            Q1=makeQuery(id+"F9.opExtrude","SWEPT_FACE",FACE,{"disambiguationData":[OSD([sQuery(id+"F8.wireOp",EDGE,"E14")])]});
            var Q2;
            Q2=makeQuery(id+"F9.opExtrude","SWEPT_FACE",FACE,{"disambiguationData":[OSD([sQuery(id+"F8.wireOp",EDGE,"E16")])]});
            fillet(context, id + "F43", {"entities" : qUnion([Q0, Q1, Q2]), "radius" : 1.27 * mm, "tangentPropagation" : true, "allowEdgeOverflow" : false});
        }
    });
